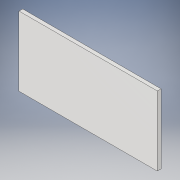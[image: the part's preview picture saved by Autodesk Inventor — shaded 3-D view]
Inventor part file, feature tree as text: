
AUTODESK INVENTOR PART (.ipt)
format: ipt  version: 2017 (Build 210142000, 142)  size: 87,040 bytes
history: native  units: in
note: dims shown in document units (in); Inventor stores cm internally (conversion verified against a paired STEP export)
features: extrude x1, sketch x1
ambient origin geometry x8: Origin, YZ Plane, XZ Plane, XY Plane, X Axis, Y Axis, Z Axis, Center Point
bodies: Solid1 (feature_tree)
feature tree (2):
  extrude  "Extrusion1"  Depth=29.5276in
  sketch  "Sketch1"  dims[d0=58.8583in d1=29.5276in d2=1.5748in d3=0.0in]
